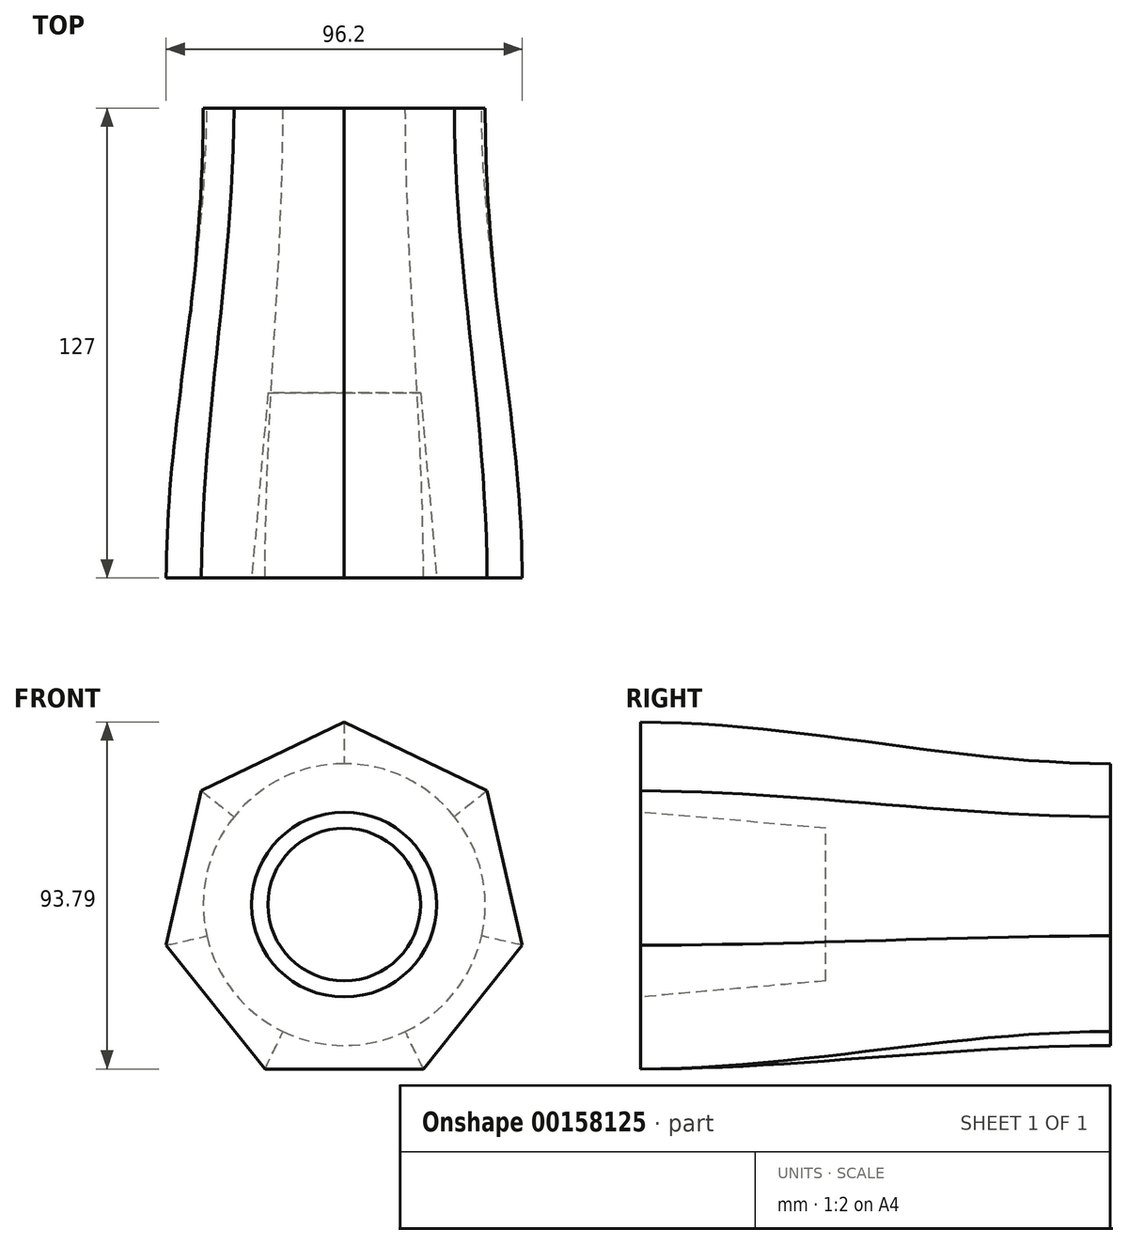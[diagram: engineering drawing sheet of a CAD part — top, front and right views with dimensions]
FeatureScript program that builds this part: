
annotation { "Feature Type Name" : "Feature", "Feature Type Description" : "" }
export const myFeature = defineFeature(function(context is Context, id is Id, definition is map)
    precondition{}
    {
        {
            var Q0;
            Q0=qCreatedBy(makeId("Front.planeOp"),FACE);
            var sketch = newSketch(context, id + "F0", { "sketchPlane" : qUnion([Q0])});
            skCircle(sketch, "E0", {"center": v(0, 0) * mm, "radius": 38.1 * mm});
            skSolve(sketch);
        }
        {
            var Q0;
            Q0=qCreatedBy(makeId("Front.planeOp"),FACE);
            cPlane(context, id + "F1", {"entities" : qUnion([Q0]), "cplaneType" : CPlaneType.OFFSET, "offset" : 127 * mm, "width" : 152.4 * mm, "height" : 152.4 * mm});
        }
        {
            var Q0;
            Q0=qCreatedBy(id+"F1.planeOp",FACE);
            var sketch = newSketch(context, id + "F2", { "sketchPlane" : qUnion([Q0])});
            skCircle(sketch, "E1.cCircle", {"center": v(0, 0) * mm, "radius": 44.45 * mm, "construction": true});
            skLineSegment(sketch, "E1.0", {"start": v(-38.57, 30.76) * mm, "end": v(0, 49.34) * mm});
            skLineSegment(sketch, "E1.1", {"start": v(0, 49.34) * mm, "end": v(38.57, 30.76) * mm});
            skLineSegment(sketch, "E1.2", {"start": v(38.57, 30.76) * mm, "end": v(48.1, -10.98) * mm});
            skLineSegment(sketch, "E1.3", {"start": v(48.1, -10.98) * mm, "end": v(21.4, -44.45) * mm});
            skLineSegment(sketch, "E1.4", {"start": v(21.4, -44.45) * mm, "end": v(-21.4, -44.45) * mm});
            skLineSegment(sketch, "E1.5", {"start": v(-21.4, -44.45) * mm, "end": v(-48.1, -10.98) * mm});
            skLineSegment(sketch, "E1.6", {"start": v(-48.1, -10.98) * mm, "end": v(-38.57, 30.76) * mm});
            skPoint(sketch, "E1.0.midPoint", {"position": v(-19.29, 40.05) * mm});
            skSolve(sketch);
        }
        {
            var Q0;
            Q0=makeQuery(id+"F2.imprint","IMPRINT",FACE,{"disambiguationData":[TD([[makeQuery(id+"F2.imprint","IMPRINT",EDGE,{"derivedFrom":sQuery(id+"F2.wireOp",EDGE,"E1.0")}),-1.0]])]});
            var Q1;
            Q1=makeQuery(id+"F0.imprint","IMPRINT",FACE,{"disambiguationData":[TD([[makeQuery(id+"F0.imprint","IMPRINT",EDGE,{"derivedFrom":sQuery(id+"F0.wireOp",EDGE,"E0")}),1.0]])]});
            loft(context, id + "F3", {"startCondition" : LoftEndDerivativeType.NORMAL_TO_PROFILE, "startMagnitude" : 1, "endCondition" : LoftEndDerivativeType.NORMAL_TO_PROFILE, "endMagnitude" : 1, "sheetProfilesArray" : [{ "sheetProfileEntities" : qUnion([Q0]) }, { "sheetProfileEntities" : qUnion([Q1]) }]});
        }
        {
            var Q0;
            Q0=makeQuery(id+"F3.opLoft","CAP_FACE",FACE,{"disambiguationData":[OSD([makeQuery(id+"F2.imprint","IMPRINT",FACE,{"disambiguationData":[TD([[makeQuery(id+"F2.imprint","IMPRINT",EDGE,{"derivedFrom":sQuery(id+"F2.wireOp",EDGE,"E1.0")}),-1.0]])]})])],"isStart":true});
            var sketch = newSketch(context, id + "F4", { "sketchPlane" : qUnion([Q0])});
            skCircle(sketch, "E2", {"center": v(0, 0) * mm, "radius": 25 * mm});
            skSolve(sketch);
        }
        {
            var Q0;
            Q0=makeQuery(id+"F4.imprint","IMPRINT",FACE,{"disambiguationData":[TD([[makeQuery(id+"F4.imprint","IMPRINT",EDGE,{"derivedFrom":sQuery(id+"F4.wireOp",EDGE,"E2")}),1.0]])]});
            extrude(context, id + "F5", {"entities" : qUnion([Q0]), "operationType" : NewBodyOperationType.REMOVE, "oppositeDirection" : true, "depth" : 50 * mm, "hasDraft" : true, "draftAngle" : 5 * degree, "draftPullDirection" : true});
        }
    });
